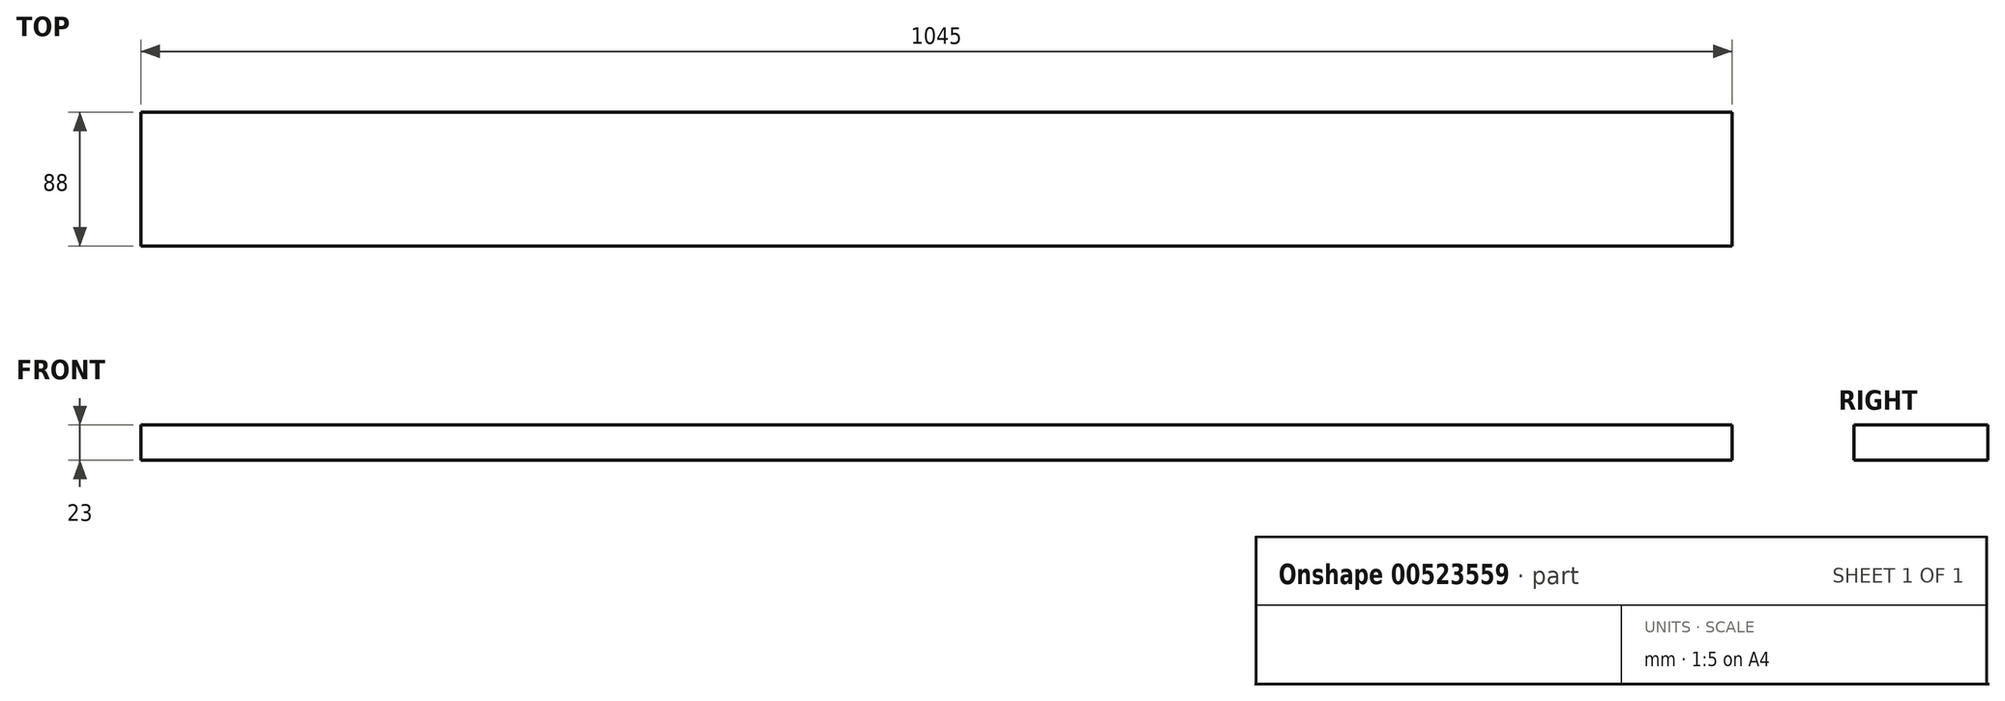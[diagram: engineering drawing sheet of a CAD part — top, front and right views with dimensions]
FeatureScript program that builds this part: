
annotation { "Feature Type Name" : "Feature", "Feature Type Description" : "" }
export const myFeature = defineFeature(function(context is Context, id is Id, definition is map)
    precondition{}
    {
        {
            var Q0;
            Q0=qCreatedBy(makeId("Top.planeOp"),FACE);
            var sketch = newSketch(context, id + "F0", { "sketchPlane" : qUnion([Q0])});
            skLineSegment(sketch, "E0.bottom", {"start": v(522.5, -44) * mm, "end": v(-522.5, -44) * mm});
            skLineSegment(sketch, "E0.top", {"start": v(522.5, 44) * mm, "end": v(-522.5, 44) * mm});
            skLineSegment(sketch, "E0.left", {"start": v(522.5, -44) * mm, "end": v(522.5, 44) * mm});
            skLineSegment(sketch, "E0.right", {"start": v(-522.5, -44) * mm, "end": v(-522.5, 44) * mm});
            skPoint(sketch, "E0.middle", {"position": v(0, 0) * mm});
            skSolve(sketch);
        }
        {
            var Q0;
            Q0 = qSketchRegion(id + "F0", true);
            extrude(context, id + "F1", {"entities" : qUnion([Q0]), "depth" : 23 * mm, "offsetDistance" : 25 * mm});
        }
    });
